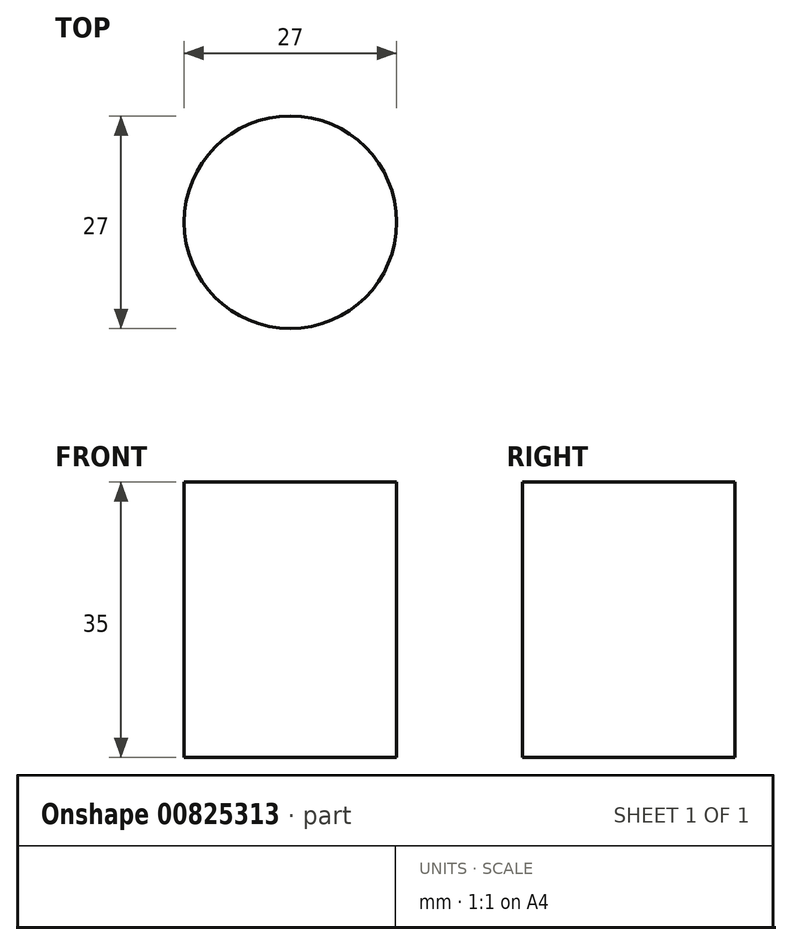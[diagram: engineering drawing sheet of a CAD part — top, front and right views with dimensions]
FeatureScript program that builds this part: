
annotation { "Feature Type Name" : "Feature", "Feature Type Description" : "" }
export const myFeature = defineFeature(function(context is Context, id is Id, definition is map)
    precondition{}
    {
        {
            var Q0;
            Q0=qCreatedBy(makeId("Top.planeOp"),FACE);
            var sketch = newSketch(context, id + "F0", { "sketchPlane" : qUnion([Q0])});
            skCircle(sketch, "E0.0", {"center": v(0, 0) * mm, "radius": 13.5 * mm});
            skSolve(sketch);
        }
        {
            var Q0;
            Q0=makeQuery(id+"F0.imprint","IMPRINT",FACE,{"disambiguationData":[TD([[makeQuery(id+"F0.imprint","IMPRINT",EDGE,{"derivedFrom":sQuery(id+"F0.wireOp",EDGE,"McCkVDBn-wuWe-QIR0-2Igs-J1055Htcdavn")}),-1.0]])]});
            var Q1;
            Q1=makeQuery(id+"F0.imprint","IMPRINT",FACE,{"disambiguationData":[TD([[makeQuery(id+"F0.imprint","IMPRINT",EDGE,{"derivedFrom":sQuery(id+"F0.wireOp",EDGE,"McCkVDBn-wuWe-QIR0-2Igs-J1055Htcdavn")}),1.0]])]});
            var Q2;
            Q2=makeQuery(id+"F0.imprint","IMPRINT",FACE,{"disambiguationData":[TD([[makeQuery(id+"F0.imprint","IMPRINT",EDGE,{"derivedFrom":sQuery(id+"F0.wireOp",EDGE,"E0.0")}),1.0]])]});
            extrude(context, id + "F1", {"entities" : qUnion([Q0, Q1, Q2]), "depth" : 35 * mm, "offsetDistance" : 25 * mm});
        }
        {
            var Q0;
            Q0=qCreatedBy(makeId("Top.planeOp"),FACE);
            var sketch = newSketch(context, id + "F2", { "sketchPlane" : qUnion([Q0])});
            skCircle(sketch, "E1", {"center": v(0, 0) * mm, "radius": 13.05 * mm});
            skSolve(sketch);
        }
        {
            var Q0;
            Q0=makeQuery(id+"F2.imprint","IMPRINT",FACE,{"disambiguationData":[TD([[makeQuery(id+"F2.imprint","IMPRINT",EDGE,{"derivedFrom":sQuery(id+"F2.wireOp",EDGE,"E1")}),1.0]])]});
            extrude(context, id + "F3", {"entities" : qUnion([Q0]), "operationType" : NewBodyOperationType.ADD, "depth" : 3 * mm, "offsetDistance" : 25 * mm});
        }
    });
